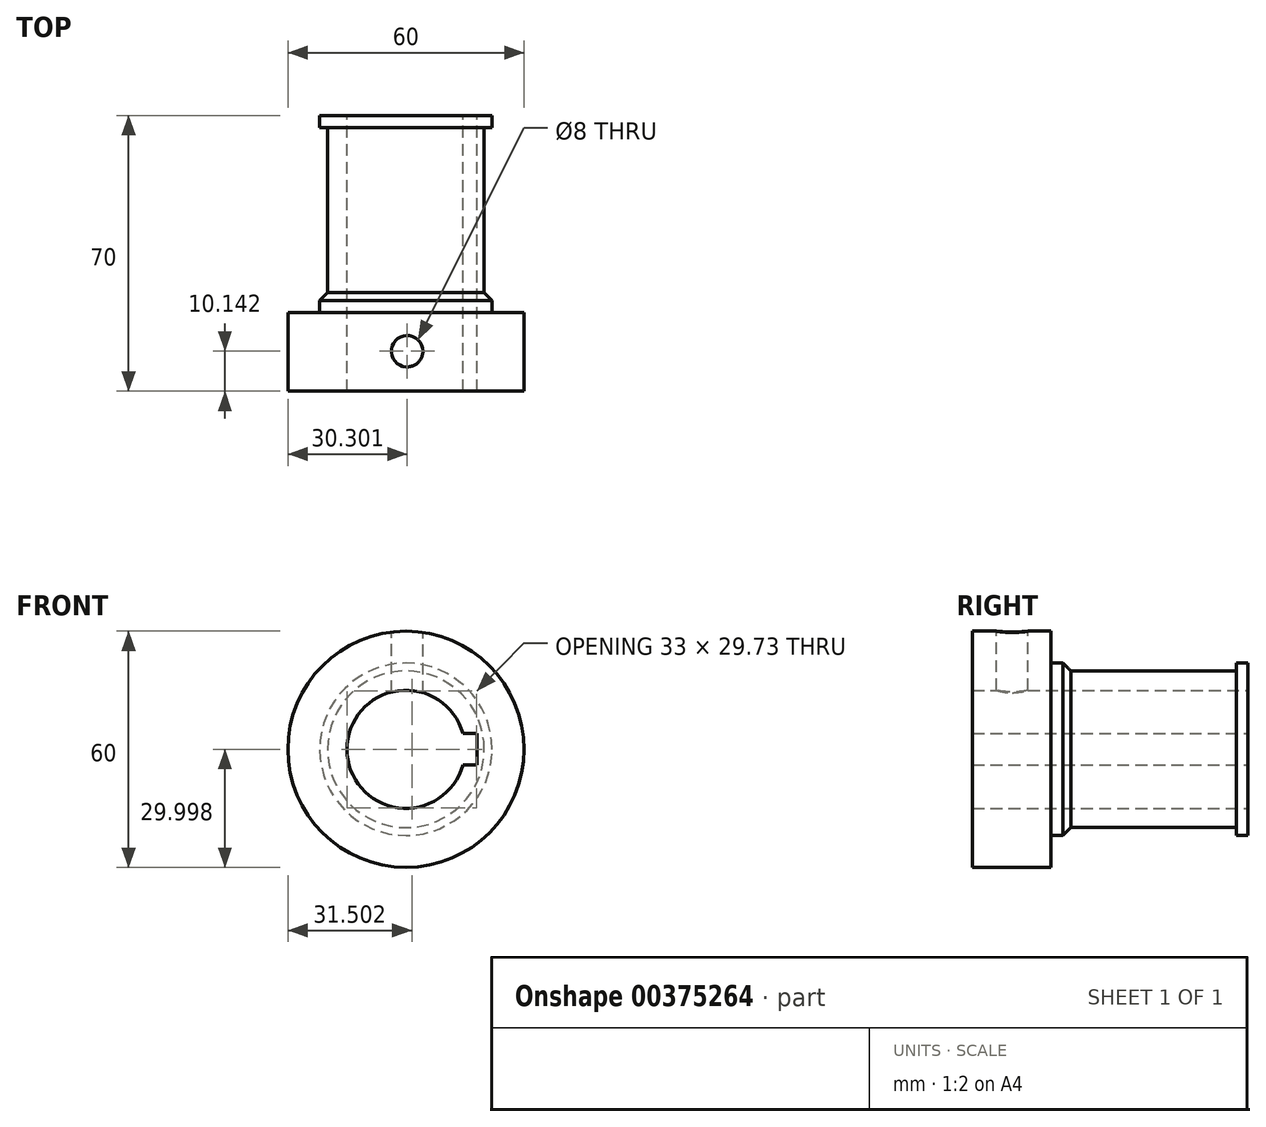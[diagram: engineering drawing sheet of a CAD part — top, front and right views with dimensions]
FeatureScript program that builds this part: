
annotation { "Feature Type Name" : "Feature", "Feature Type Description" : "" }
export const myFeature = defineFeature(function(context is Context, id is Id, definition is map)
    precondition{}
    {
        {
            var Q0;
            Q0=qCreatedBy(makeId("Front.planeOp"),FACE);
            var sketch = newSketch(context, id + "F0", { "sketchPlane" : qUnion([Q0])});
            skCircle(sketch, "E0", {"center": v(61.74, 67.36) * mm, "radius": 30 * mm});
            skSolve(sketch);
        }
        {
            var Q0;
            Q0=makeQuery(id+"F0.imprint","IMPRINT",FACE,{"disambiguationData":[TD([[makeQuery(id+"F0.imprint","IMPRINT",EDGE,{"derivedFrom":sQuery(id+"F0.wireOp",EDGE,"E0")}),1.0]])]});
            extrude(context, id + "F1", {"entities" : qUnion([Q0]), "depth" : 20 * mm});
        }
        {
            var Q0;
            Q0=makeQuery(id+"F1.opExtrude","CAP_FACE",FACE,{"disambiguationData":[OSD([sQuery(id+"F0.wireOp",EDGE,"E0")])],"isStart":true});
            var sketch = newSketch(context, id + "F2", { "sketchPlane" : qUnion([Q0])});
            skCircle(sketch, "E1", {"center": v(-61.74, 67.36) * mm, "radius": 21.9 * mm});
            skSolve(sketch);
        }
        {
            var Q0;
            Q0=makeQuery(id+"F2.imprint","IMPRINT",FACE,{"disambiguationData":[TD([[makeQuery(id+"F2.imprint","IMPRINT",EDGE,{"derivedFrom":sQuery(id+"F2.wireOp",EDGE,"E1")}),1.0]])]});
            extrude(context, id + "F3", {"entities" : qUnion([Q0]), "operationType" : NewBodyOperationType.ADD, "depth" : 5 * mm});
        }
        {
            var Q0;
            Q0=makeQuery(id+"F3.opExtrude","CAP_EDGE",EDGE,{"disambiguationData":[OSD([sQuery(id+"F2.wireOp",EDGE,"E1")])],"isStart":false});
            chamfer(context, id + "F4", {"entities" : qUnion([Q0]), "width" : 2 * mm, "tangentPropagation" : true});
        }
        {
            var Q0;
            Q0=makeQuery(id+"F3.opExtrude","CAP_FACE",FACE,{"disambiguationData":[OSD([sQuery(id+"F2.wireOp",EDGE,"E1")])],"isStart":false});
            extrude(context, id + "F5", {"entities" : qUnion([Q0]), "operationType" : NewBodyOperationType.ADD, "depth" : 42 * mm});
        }
        {
            var Q0;
            Q0=makeQuery(id+"F5.opExtrude","CAP_FACE",FACE,{"disambiguationData":[OSD([sQuery(id+"F2.wireOp",EDGE,"E1")])],"isStart":false});
            var sketch = newSketch(context, id + "F6", { "sketchPlane" : qUnion([Q0])});
            skCircle(sketch, "E2", {"center": v(-61.74, 67.36) * mm, "radius": 21.9 * mm});
            skSolve(sketch);
        }
        {
            var Q0;
            Q0=makeQuery(id+"F6.imprint","IMPRINT",FACE,{"disambiguationData":[TD([[makeQuery(id+"F6.imprint","IMPRINT",EDGE,{"derivedFrom":makeQuery(id+"F5.opExtrude","CAP_EDGE",EDGE,{"disambiguationData":[OSD([sQuery(id+"F2.wireOp",EDGE,"E1")])],"isStart":false})}),1.0]])]});
            var Q1;
            Q1=makeQuery(id+"F6.imprint","IMPRINT",FACE,{"disambiguationData":[TD([[makeQuery(id+"F6.imprint","IMPRINT",EDGE,{"derivedFrom":sQuery(id+"F6.wireOp",EDGE,"E2")}),1.0]])]});
            extrude(context, id + "F7", {"entities" : qUnion([Q0, Q1]), "operationType" : NewBodyOperationType.ADD, "depth" : 3 * mm});
        }
        {
            var Q0;
            Q0=makeQuery(id+"F7.opExtrude","CAP_FACE",FACE,{"disambiguationData":[OSD([sQuery(id+"F6.wireOp",EDGE,"E2")])],"isStart":false});
            var sketch = newSketch(context, id + "F8", { "sketchPlane" : qUnion([Q0])});
            skArc(sketch, "E3", {"start": v(-76.2, 63.36) * mm, "mid": v(-46.74, 67.36) * mm, "end": v(-76.2, 71.36) * mm});
            skLineSegment(sketch, "E4", {"start": v(-79.74, 67.36) * mm, "end": v(-79.74, 71.36) * mm});
            skLineSegment(sketch, "E5", {"start": v(-79.74, 71.36) * mm, "end": v(-76.2, 71.36) * mm});
            skLineSegment(sketch, "E6", {"start": v(-79.74, 67.36) * mm, "end": v(-79.74, 63.36) * mm});
            skLineSegment(sketch, "E7", {"start": v(-79.74, 63.36) * mm, "end": v(-76.2, 63.36) * mm});
            skPoint(sketch, "E8.start.orphan", {"position": v(-46.74, 67.36) * mm});
            skSolve(sketch);
        }
        {
            var Q0;
            Q0=makeQuery(id+"F8.imprint","IMPRINT",FACE,{"disambiguationData":[TD([[makeQuery(id+"F8.imprint","IMPRINT",EDGE,{"derivedFrom":sQuery(id+"F8.wireOp",EDGE,"E3")}),1.0]])]});
            extrude(context, id + "F9", {"entities" : qUnion([Q0]), "operationType" : NewBodyOperationType.REMOVE, "oppositeDirection" : true, "depth" : 74.3 * mm});
        }
        {
            var Q0;
            Q0=qCreatedBy(makeId("Top.planeOp"),FACE);
            cPlane(context, id + "F10", {"entities" : qUnion([Q0]), "cplaneType" : CPlaneType.OFFSET, "offset" : 100 * mm, "width" : 150 * mm, "height" : 150 * mm});
        }
        {
            var Q0;
            Q0=qCreatedBy(id+"F10.planeOp",FACE);
            var sketch = newSketch(context, id + "F11", { "sketchPlane" : qUnion([Q0])});
            skCircle(sketch, "E9", {"center": v(62.04, -9.86) * mm, "radius": 4 * mm});
            skSolve(sketch);
        }
        {
            var Q0;
            Q0=makeQuery(id+"F11.imprint","IMPRINT",FACE,{"disambiguationData":[TD([[makeQuery(id+"F11.imprint","IMPRINT",EDGE,{"derivedFrom":sQuery(id+"F11.wireOp",EDGE,"E9")}),1.0]])]});
            extrude(context, id + "F12", {"entities" : qUnion([Q0]), "operationType" : NewBodyOperationType.REMOVE, "oppositeDirection" : true, "depth" : 25 * mm});
        }
    });
